# Revit family: PRD_FrankeWS_Cn-oprtdLcks_AQUAPAYCoin-operatedController_AQUA801_AQUA803
name_source: partatom
category: Plumbing Fixtures
revit_build: Autodesk Revit 2018 (Build: 20190510_1515(x64)
units: mm (PartAtom-declared; Revit-internal decimal feet)

## family parameters
Cut with Voids When Loaded = Yes
Host = Face
OmniClass Number = 23.45.05.14.99
OmniClass Title = Other Sanitary Washing Plumbing Fixtures
Part Type = Normal
Room Calculation Point = No
Round Connector Dimension = Use Diameter
Shared = Yes

## types (2) — shared parameters
Application = Shower taps
AssetType = Fixed
Category = Pr_30_36_08_15, Coin-operated locks
Default Elevation = 1100 mm
DurationUnit = year
Finish = rugged
GeneralMaterial = PRD_AR_StainlessSteel_Rugged
GrossWeight = 3.97 kg
IfcExportAs = IfcControllerType
IfcExportType = USERDEFINED
Manufacturer = KWC Group AG
ManufacturerName = KWC Group AG
ManufacturerURL = www.kwc.com
Material = Stainless steel
NetWeight = 3.53 kg
NominalDepth = 130 mm  [stored 0.426509 ft]
NominalHeight = 220 mm  [stored 0.721785 ft]
NominalWidth = 240 mm  [stored 0.787402 ft]
PowerSupplyConnection = 24 V DC
ProductInformation = https://pim.kwc.com
ProtectiveSystemIP = 22
Shape = Cuboid
Size = 240 x 220 x 130 mm (W x H x D)
Status = New
TokenCoin = 0.5
URL = www.kwc.com
Uniclass2015Code = Pr_30_36_08_15
Uniclass2015Title = Coin-operated locks
Uniclass2015Version = Products v1.17
Version = 1
WarrantyDurationUnit = year

## per-type parameters (varying)
| type | AQUA801 | AQUA803 | BIMObjectName | Description | Features | ModelNumber | Name | PowerConsumption | ProductCode |
| AQUA801 | Yes | No | PRD_AR_Coin-operatedLocks_AQUAPAYCoin-operatedController_AQUA801 | AQUAPAY coin-operated controller for chargeable water delivery for controlling one A3000 open shower fitting. Shower duration for one coin is selectable in steps of one second up to a total of 8 minutes, preset to 3 minutes. Automatic interruption of shower-duration when water is not being withdrawn. Rugged stainless steel housing for on-wall mounting with safety lock. Model for coins EURO 0.50, 24 V DC. | controlling one A3000 open shower fitting | 2000100342 | AQUAPAY Coin-operated controller AQUA801 | 3 | 210.0636.621 |
| AQUA803 | No | Yes | PRD_AR_Coin-operatedLocks_AQUAPAYCoin-operatedController_AQUA803 | AQUAPAY coin-operated controller for chargeable water delivery for controlling 2 - 31 A3000 open shower fittings. Display for user guide and showing free showers, selectable via key. Shower duration for one coin is selectable in steps of one second up to a total of 8 minutes, preset to 3 minutes. Automatic interruption of shower-duration when water is not being withdrawn. Rugged stainless steel housing for on-wall mounting with safety lock. Model for coins EURO 0.50, 24 V DC. | controlling 2 - 31 A3000 open shower fittings | 2000100419 | AQUAPAY Coin-operated controller AQUA803 | 10 | 210.0636.622 |

note: column(s) folded — value = type name in every type: Model, ModelReference

note: [stored X ft] marks values corroborated as IEEE doubles in the binary element streams (Revit-internal decimal feet)

## geometry (parser evidence)
native form markers: Sweep x4
no freeform markers — native parametric forms only
